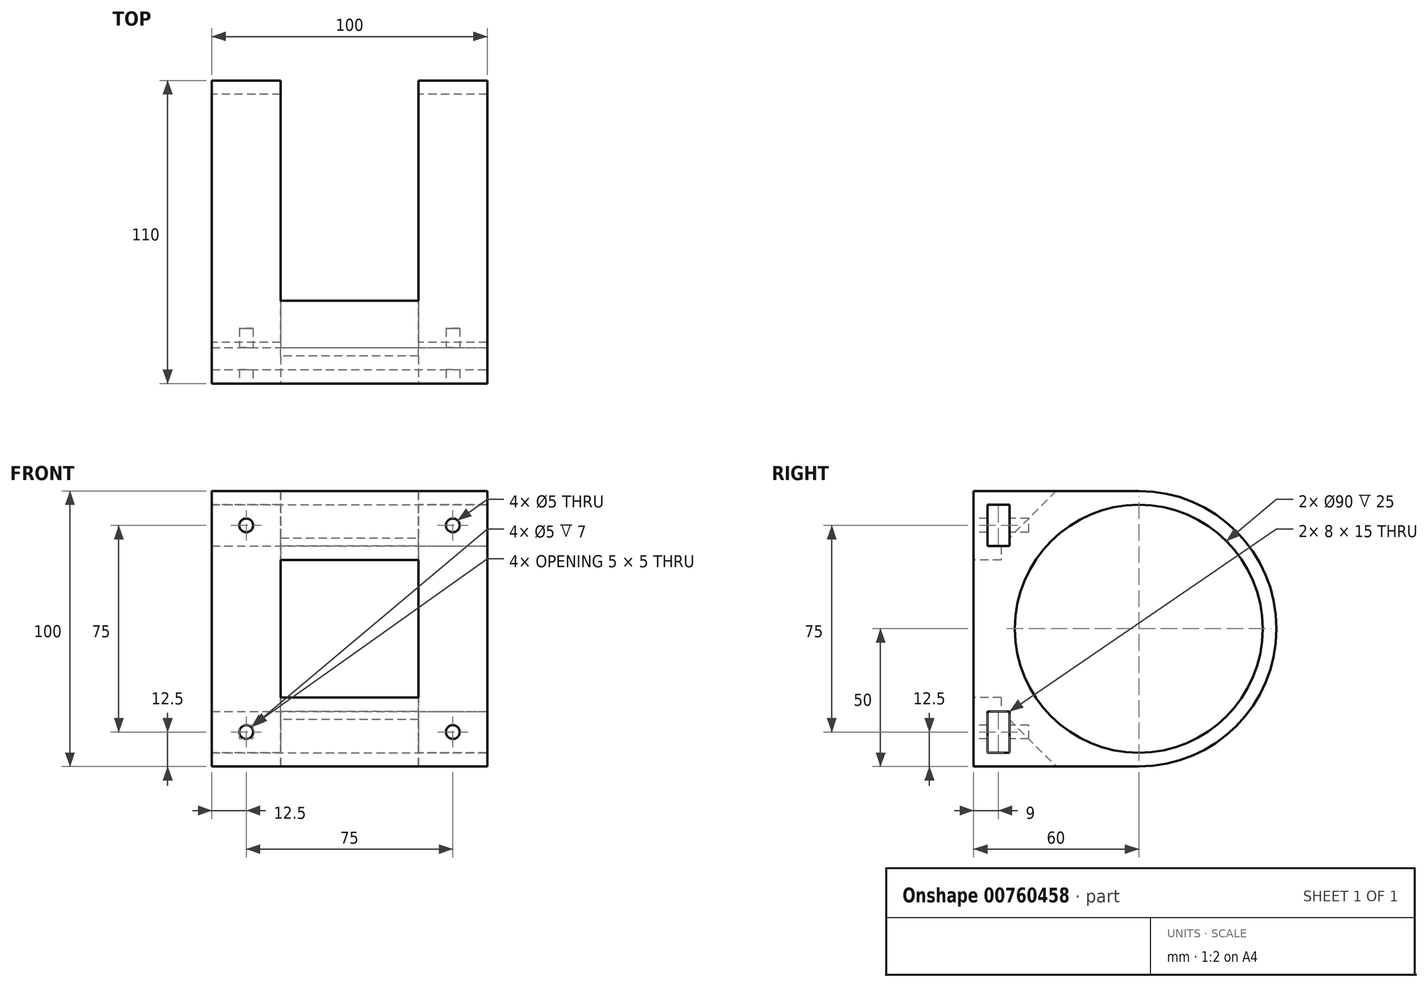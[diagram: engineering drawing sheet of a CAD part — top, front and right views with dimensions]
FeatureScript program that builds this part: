
annotation { "Feature Type Name" : "Feature", "Feature Type Description" : "" }
export const myFeature = defineFeature(function(context is Context, id is Id, definition is map)
    precondition{}
    {
        {
            var Q0;
            Q0=qCreatedBy(makeId("Right.planeOp"),FACE);
            var sketch = newSketch(context, id + "F0", { "sketchPlane" : qUnion([Q0])});
            skCircle(sketch, "E0", {"center": v(0, 0) * mm, "radius": 50 * mm});
            skCircle(sketch, "E1", {"center": v(0, 0) * mm, "radius": 40 * mm});
            skCircle(sketch, "E2", {"center": v(0, 0) * mm, "radius": 45 * mm});
            skLineSegment(sketch, "E3", {"start": v(-45, 0) * mm, "end": v(45, 0) * mm});
            skLineSegment(sketch, "E4.1.0", {"start": v(-44.14, -8.78) * mm, "end": v(44.14, 8.78) * mm});
            skLineSegment(sketch, "E4.2.0", {"start": v(-41.57, -17.22) * mm, "end": v(41.57, 17.22) * mm});
            skLineSegment(sketch, "E4.3.0", {"start": v(-37.42, -25) * mm, "end": v(37.42, 25) * mm});
            skLineSegment(sketch, "E4.4.0", {"start": v(-31.82, -31.82) * mm, "end": v(31.82, 31.82) * mm});
            skLineSegment(sketch, "E4.5.0", {"start": v(-25, -37.42) * mm, "end": v(25, 37.42) * mm});
            skLineSegment(sketch, "E4.6.0", {"start": v(-17.22, -41.57) * mm, "end": v(17.22, 41.57) * mm});
            skLineSegment(sketch, "E4.7.0", {"start": v(-8.78, -44.14) * mm, "end": v(8.78, 44.14) * mm});
            skLineSegment(sketch, "E4.8.0", {"start": v(0, -45) * mm, "end": v(0, 45) * mm});
            skLineSegment(sketch, "E4.9.0", {"start": v(8.78, -44.14) * mm, "end": v(-8.78, 44.14) * mm});
            skLineSegment(sketch, "E4.10.0", {"start": v(17.22, -41.57) * mm, "end": v(-17.22, 41.57) * mm});
            skLineSegment(sketch, "E4.11.0", {"start": v(25, -37.42) * mm, "end": v(-25, 37.42) * mm});
            skLineSegment(sketch, "E4.12.0", {"start": v(31.82, -31.82) * mm, "end": v(-31.82, 31.82) * mm});
            skLineSegment(sketch, "E4.13.0", {"start": v(37.42, -25) * mm, "end": v(-37.42, 25) * mm});
            skLineSegment(sketch, "E4.14.0", {"start": v(41.57, -17.22) * mm, "end": v(-41.57, 17.22) * mm});
            skLineSegment(sketch, "E4.15.0", {"start": v(44.14, -8.78) * mm, "end": v(-44.14, 8.78) * mm});
            skLineSegment(sketch, "E4.16.0", {"start": v(45, 0) * mm, "end": v(-45, 0) * mm});
            skLineSegment(sketch, "E4.17.0", {"start": v(44.14, 8.78) * mm, "end": v(-44.14, -8.78) * mm});
            skLineSegment(sketch, "E4.18.0", {"start": v(41.57, 17.22) * mm, "end": v(-41.57, -17.22) * mm});
            skLineSegment(sketch, "E4.19.0", {"start": v(37.42, 25) * mm, "end": v(-37.42, -25) * mm});
            skLineSegment(sketch, "E4.20.0", {"start": v(31.82, 31.82) * mm, "end": v(-31.82, -31.82) * mm});
            skLineSegment(sketch, "E4.21.0", {"start": v(25, 37.42) * mm, "end": v(-25, -37.42) * mm});
            skLineSegment(sketch, "E4.22.0", {"start": v(17.22, 41.57) * mm, "end": v(-17.22, -41.57) * mm});
            skLineSegment(sketch, "E4.23.0", {"start": v(8.78, 44.14) * mm, "end": v(-8.78, -44.14) * mm});
            skLineSegment(sketch, "E4.24.0", {"start": v(0, 45) * mm, "end": v(0, -45) * mm});
            skLineSegment(sketch, "E4.25.0", {"start": v(-8.78, 44.14) * mm, "end": v(8.78, -44.14) * mm});
            skLineSegment(sketch, "E4.26.0", {"start": v(-17.22, 41.57) * mm, "end": v(17.22, -41.57) * mm});
            skLineSegment(sketch, "E4.27.0", {"start": v(-25, 37.42) * mm, "end": v(25, -37.42) * mm});
            skLineSegment(sketch, "E4.28.0", {"start": v(-31.82, 31.82) * mm, "end": v(31.82, -31.82) * mm});
            skLineSegment(sketch, "E4.29.0", {"start": v(-37.42, 25) * mm, "end": v(37.42, -25) * mm});
            skLineSegment(sketch, "E4.30.0", {"start": v(-41.57, 17.22) * mm, "end": v(41.57, -17.22) * mm});
            skLineSegment(sketch, "E4.31.0", {"start": v(-44.14, 8.78) * mm, "end": v(44.14, -8.78) * mm});
            skLineSegment(sketch, "E5.bottom", {"start": v(0, 50) * mm, "end": v(-60, 50) * mm});
            skLineSegment(sketch, "E5.top", {"start": v(0, -50) * mm, "end": v(-60, -50) * mm});
            skLineSegment(sketch, "E5.left", {"start": v(0, 50) * mm, "end": v(0, -50) * mm, "construction": true});
            skLineSegment(sketch, "E5.right", {"start": v(-60, 50) * mm, "end": v(-60, -50) * mm});
            skLineSegment(sketch, "E6", {"start": v(-50, 50) * mm, "end": v(-50, -50) * mm});
            skLineSegment(sketch, "E7", {"start": v(-30, 50) * mm, "end": v(-50, 30) * mm});
            skLineSegment(sketch, "E8", {"start": v(-50, -30) * mm, "end": v(-30, -50) * mm});
            skSolve(sketch);
        }
        {
            var Q0;
            {var subQ0=sQuery(id+"F0.wireOp",EDGE,"E5.bottom");Q0=makeQuery(id+"F0.imprint","IMPRINT",FACE,{"disambiguationData":[TD([[makeQuery(id+"F0.imprint","IMPRINT",EDGE,{"derivedFrom":subQ0}),1.0]])]});}
            var Q1;
            {var subQ15=sQuery(id+"F0.wireOp",EDGE,"E0");var subQ16=makeQuery(id+"F0.imprint","INTERSECT",VERTEX,{"derivedFrom":[subQ15,sQuery(id+"F0.wireOp",EDGE,"E5.bottom")]});Q1=makeQuery(id+"F0.imprint","IMPRINT",FACE,{"disambiguationData":[TD([[makeQuery(id+"F0.imprint","IMPRINT",EDGE,{"disambiguationData":[TD([[subQ16,-1.0]])],"derivedFrom":subQ15}),1.0]])]});}
            var Q2;
            {var subQ0=sQuery(id+"F0.wireOp",EDGE,"E4.25.0");var subQ1=sQuery(id+"F0.wireOp",EDGE,"E1");var subQ2=makeQuery(id+"F0.imprint","INTERSECT",VERTEX,{"disambiguationData":[OD(0.0)],"derivedFrom":[subQ1,subQ0]});Q2=makeQuery(id+"F0.imprint","IMPRINT",FACE,{"disambiguationData":[TD([[makeQuery(id+"F0.imprint","IMPRINT",EDGE,{"disambiguationData":[TD([[subQ2,-1.0]])],"derivedFrom":subQ1}),-1.0]])]});}
            var Q3;
            {var subQ0=sQuery(id+"F0.wireOp",EDGE,"E4.26.0");var subQ1=sQuery(id+"F0.wireOp",EDGE,"E1");var subQ2=makeQuery(id+"F0.imprint","INTERSECT",VERTEX,{"disambiguationData":[OD(0.0)],"derivedFrom":[subQ1,subQ0]});Q3=makeQuery(id+"F0.imprint","IMPRINT",FACE,{"disambiguationData":[TD([[makeQuery(id+"F0.imprint","IMPRINT",EDGE,{"disambiguationData":[TD([[subQ2,-1.0]])],"derivedFrom":subQ1}),-1.0]])]});}
            var Q4;
            {var subQ0=sQuery(id+"F0.wireOp",EDGE,"E4.29.0");var subQ1=sQuery(id+"F0.wireOp",EDGE,"E1");var subQ2=makeQuery(id+"F0.imprint","INTERSECT",VERTEX,{"disambiguationData":[OD(0.0)],"derivedFrom":[subQ1,subQ0]});Q4=makeQuery(id+"F0.imprint","IMPRINT",FACE,{"disambiguationData":[TD([[makeQuery(id+"F0.imprint","IMPRINT",EDGE,{"disambiguationData":[TD([[subQ2,-1.0]])],"derivedFrom":subQ1}),-1.0]])]});}
            var Q5;
            {var subQ0=sQuery(id+"F0.wireOp",EDGE,"E4.30.0");var subQ1=sQuery(id+"F0.wireOp",EDGE,"E1");var subQ2=makeQuery(id+"F0.imprint","INTERSECT",VERTEX,{"disambiguationData":[OD(0.0)],"derivedFrom":[subQ1,subQ0]});Q5=makeQuery(id+"F0.imprint","IMPRINT",FACE,{"disambiguationData":[TD([[makeQuery(id+"F0.imprint","IMPRINT",EDGE,{"disambiguationData":[TD([[subQ2,-1.0]])],"derivedFrom":subQ1}),-1.0]])]});}
            var Q6;
            {var subQ0=sQuery(id+"F0.wireOp",EDGE,"E4.17.0");var subQ1=sQuery(id+"F0.wireOp",EDGE,"E1");var subQ2=makeQuery(id+"F0.imprint","INTERSECT",VERTEX,{"disambiguationData":[OD(1.0)],"derivedFrom":[subQ1,subQ0]});Q6=makeQuery(id+"F0.imprint","IMPRINT",FACE,{"disambiguationData":[TD([[makeQuery(id+"F0.imprint","IMPRINT",EDGE,{"disambiguationData":[TD([[subQ2,-1.0]])],"derivedFrom":subQ1}),-1.0]])]});}
            var Q7;
            {var subQ0=sQuery(id+"F0.wireOp",EDGE,"E4.18.0");var subQ1=sQuery(id+"F0.wireOp",EDGE,"E1");var subQ2=makeQuery(id+"F0.imprint","INTERSECT",VERTEX,{"disambiguationData":[OD(1.0)],"derivedFrom":[subQ1,subQ0]});Q7=makeQuery(id+"F0.imprint","IMPRINT",FACE,{"disambiguationData":[TD([[makeQuery(id+"F0.imprint","IMPRINT",EDGE,{"disambiguationData":[TD([[subQ2,-1.0]])],"derivedFrom":subQ1}),-1.0]])]});}
            var Q8;
            {var subQ0=sQuery(id+"F0.wireOp",EDGE,"E4.21.0");var subQ1=sQuery(id+"F0.wireOp",EDGE,"E1");var subQ2=makeQuery(id+"F0.imprint","INTERSECT",VERTEX,{"disambiguationData":[OD(1.0)],"derivedFrom":[subQ1,subQ0]});Q8=makeQuery(id+"F0.imprint","IMPRINT",FACE,{"disambiguationData":[TD([[makeQuery(id+"F0.imprint","IMPRINT",EDGE,{"disambiguationData":[TD([[subQ2,-1.0]])],"derivedFrom":subQ1}),-1.0]])]});}
            var Q9;
            {var subQ0=sQuery(id+"F0.wireOp",EDGE,"E4.22.0");var subQ1=sQuery(id+"F0.wireOp",EDGE,"E1");var subQ2=makeQuery(id+"F0.imprint","INTERSECT",VERTEX,{"disambiguationData":[OD(1.0)],"derivedFrom":[subQ1,subQ0]});Q9=makeQuery(id+"F0.imprint","IMPRINT",FACE,{"disambiguationData":[TD([[makeQuery(id+"F0.imprint","IMPRINT",EDGE,{"disambiguationData":[TD([[subQ2,-1.0]])],"derivedFrom":subQ1}),-1.0]])]});}
            var Q10;
            {var subQ0=sQuery(id+"F0.wireOp",EDGE,"E4.25.0");var subQ1=sQuery(id+"F0.wireOp",EDGE,"E1");var subQ2=makeQuery(id+"F0.imprint","INTERSECT",VERTEX,{"disambiguationData":[OD(1.0)],"derivedFrom":[subQ1,subQ0]});Q10=makeQuery(id+"F0.imprint","IMPRINT",FACE,{"disambiguationData":[TD([[makeQuery(id+"F0.imprint","IMPRINT",EDGE,{"disambiguationData":[TD([[subQ2,-1.0]])],"derivedFrom":subQ1}),-1.0]])]});}
            var Q11;
            {var subQ0=sQuery(id+"F0.wireOp",EDGE,"E4.26.0");var subQ1=sQuery(id+"F0.wireOp",EDGE,"E1");var subQ2=makeQuery(id+"F0.imprint","INTERSECT",VERTEX,{"disambiguationData":[OD(1.0)],"derivedFrom":[subQ1,subQ0]});Q11=makeQuery(id+"F0.imprint","IMPRINT",FACE,{"disambiguationData":[TD([[makeQuery(id+"F0.imprint","IMPRINT",EDGE,{"disambiguationData":[TD([[subQ2,-1.0]])],"derivedFrom":subQ1}),-1.0]])]});}
            var Q12;
            {var subQ0=sQuery(id+"F0.wireOp",EDGE,"E4.29.0");var subQ1=sQuery(id+"F0.wireOp",EDGE,"E1");var subQ2=makeQuery(id+"F0.imprint","INTERSECT",VERTEX,{"disambiguationData":[OD(1.0)],"derivedFrom":[subQ1,subQ0]});Q12=makeQuery(id+"F0.imprint","IMPRINT",FACE,{"disambiguationData":[TD([[makeQuery(id+"F0.imprint","IMPRINT",EDGE,{"disambiguationData":[TD([[subQ2,-1.0]])],"derivedFrom":subQ1}),-1.0]])]});}
            var Q13;
            {var subQ0=sQuery(id+"F0.wireOp",EDGE,"E4.30.0");var subQ1=sQuery(id+"F0.wireOp",EDGE,"E1");var subQ2=makeQuery(id+"F0.imprint","INTERSECT",VERTEX,{"disambiguationData":[OD(1.0)],"derivedFrom":[subQ1,subQ0]});Q13=makeQuery(id+"F0.imprint","IMPRINT",FACE,{"disambiguationData":[TD([[makeQuery(id+"F0.imprint","IMPRINT",EDGE,{"disambiguationData":[TD([[subQ2,-1.0]])],"derivedFrom":subQ1}),-1.0]])]});}
            var Q14;
            {var subQ0=sQuery(id+"F0.wireOp",EDGE,"E4.17.0");var subQ1=sQuery(id+"F0.wireOp",EDGE,"E1");var subQ2=makeQuery(id+"F0.imprint","INTERSECT",VERTEX,{"disambiguationData":[OD(0.0)],"derivedFrom":[subQ1,subQ0]});Q14=makeQuery(id+"F0.imprint","IMPRINT",FACE,{"disambiguationData":[TD([[makeQuery(id+"F0.imprint","IMPRINT",EDGE,{"disambiguationData":[TD([[subQ2,-1.0]])],"derivedFrom":subQ1}),-1.0]])]});}
            var Q15;
            {var subQ0=sQuery(id+"F0.wireOp",EDGE,"E4.18.0");var subQ1=sQuery(id+"F0.wireOp",EDGE,"E1");var subQ2=makeQuery(id+"F0.imprint","INTERSECT",VERTEX,{"disambiguationData":[OD(0.0)],"derivedFrom":[subQ1,subQ0]});Q15=makeQuery(id+"F0.imprint","IMPRINT",FACE,{"disambiguationData":[TD([[makeQuery(id+"F0.imprint","IMPRINT",EDGE,{"disambiguationData":[TD([[subQ2,-1.0]])],"derivedFrom":subQ1}),-1.0]])]});}
            var Q16;
            {var subQ0=sQuery(id+"F0.wireOp",EDGE,"E4.21.0");var subQ1=sQuery(id+"F0.wireOp",EDGE,"E1");var subQ2=makeQuery(id+"F0.imprint","INTERSECT",VERTEX,{"disambiguationData":[OD(0.0)],"derivedFrom":[subQ1,subQ0]});Q16=makeQuery(id+"F0.imprint","IMPRINT",FACE,{"disambiguationData":[TD([[makeQuery(id+"F0.imprint","IMPRINT",EDGE,{"disambiguationData":[TD([[subQ2,-1.0]])],"derivedFrom":subQ1}),-1.0]])]});}
            var Q17;
            {var subQ0=sQuery(id+"F0.wireOp",EDGE,"E4.22.0");var subQ1=sQuery(id+"F0.wireOp",EDGE,"E1");var subQ2=makeQuery(id+"F0.imprint","INTERSECT",VERTEX,{"disambiguationData":[OD(0.0)],"derivedFrom":[subQ1,subQ0]});Q17=makeQuery(id+"F0.imprint","IMPRINT",FACE,{"disambiguationData":[TD([[makeQuery(id+"F0.imprint","IMPRINT",EDGE,{"disambiguationData":[TD([[subQ2,-1.0]])],"derivedFrom":subQ1}),-1.0]])]});}
            var Q18;
            {var subQ4=sQuery(id+"F0.wireOp",EDGE,"E5.right");Q18=makeQuery(id+"F0.imprint","IMPRINT",FACE,{"disambiguationData":[TD([[makeQuery(id+"F0.imprint","IMPRINT",EDGE,{"derivedFrom":subQ4}),1.0]])]});}
            var Q19;
            {var subQ0=sQuery(id+"F0.wireOp",EDGE,"E5.top");var subQ1=sQuery(id+"F0.wireOp",EDGE,"E0");var subQ2=makeQuery(id+"F0.imprint","INTERSECT",VERTEX,{"derivedFrom":[subQ1,subQ0]});Q19=makeQuery(id+"F0.imprint","IMPRINT",FACE,{"disambiguationData":[TD([[makeQuery(id+"F0.imprint","IMPRINT",EDGE,{"disambiguationData":[TD([[subQ2,1.0]])],"derivedFrom":subQ1}),-1.0]])]});}
            var Q20;
            {var subQ5=sQuery(id+"F0.wireOp",EDGE,"E7");Q20=makeQuery(id+"F0.imprint","IMPRINT",FACE,{"disambiguationData":[TD([[makeQuery(id+"F0.imprint","IMPRINT",EDGE,{"derivedFrom":subQ5}),1.0]])]});}
            var Q21;
            {var subQ3=sQuery(id+"F0.wireOp",EDGE,"E8");Q21=makeQuery(id+"F0.imprint","IMPRINT",FACE,{"disambiguationData":[TD([[makeQuery(id+"F0.imprint","IMPRINT",EDGE,{"derivedFrom":subQ3}),-1.0]])]});}
            extrude(context, id + "F1", {"entities" : qUnion([Q0, Q1, Q2, Q3, Q4, Q5, Q6, Q7, Q8, Q9, Q10, Q11, Q12, Q13, Q14, Q15, Q16, Q17, Q18, Q19, Q20, Q21]), "endBound" : BoundingType.SYMMETRIC, "depth" : 100 * mm, "offsetDistance" : 25 * mm});
        }
        {
            var Q0;
            {var subQ15=sQuery(id+"F0.wireOp",EDGE,"E0");var subQ16=makeQuery(id+"F0.imprint","INTERSECT",VERTEX,{"derivedFrom":[subQ15,sQuery(id+"F0.wireOp",EDGE,"E5.bottom")]});Q0=makeQuery(id+"F0.imprint","IMPRINT",FACE,{"disambiguationData":[TD([[makeQuery(id+"F0.imprint","IMPRINT",EDGE,{"disambiguationData":[TD([[subQ16,-1.0]])],"derivedFrom":subQ15}),1.0]])]});}
            var Q1;
            {var subQ0=sQuery(id+"F0.wireOp",EDGE,"E4.23.0");var subQ1=sQuery(id+"F0.wireOp",EDGE,"E1");var subQ2=makeQuery(id+"F0.imprint","INTERSECT",VERTEX,{"disambiguationData":[OD(1.0)],"derivedFrom":[subQ1,subQ0]});Q1=makeQuery(id+"F0.imprint","IMPRINT",FACE,{"disambiguationData":[TD([[makeQuery(id+"F0.imprint","IMPRINT",EDGE,{"disambiguationData":[TD([[subQ2,-1.0]])],"derivedFrom":subQ1}),-1.0]])]});}
            var Q2;
            {var subQ0=sQuery(id+"F0.wireOp",EDGE,"E4.17.0");var subQ1=sQuery(id+"F0.wireOp",EDGE,"E1");var subQ2=makeQuery(id+"F0.imprint","INTERSECT",VERTEX,{"disambiguationData":[OD(0.0)],"derivedFrom":[subQ1,subQ0]});Q2=makeQuery(id+"F0.imprint","IMPRINT",FACE,{"disambiguationData":[TD([[makeQuery(id+"F0.imprint","IMPRINT",EDGE,{"disambiguationData":[TD([[subQ2,1.0]])],"derivedFrom":subQ1}),1.0]])]});}
            var Q3;
            {var subQ0=sQuery(id+"F0.wireOp",EDGE,"E4.16.0");var subQ1=sQuery(id+"F0.wireOp",EDGE,"E1");var subQ2=makeQuery(id+"F0.imprint","INTERSECT",VERTEX,{"disambiguationData":[OD(0.0)],"derivedFrom":[subQ1,subQ0]});Q3=makeQuery(id+"F0.imprint","IMPRINT",FACE,{"disambiguationData":[TD([[makeQuery(id+"F0.imprint","IMPRINT",EDGE,{"disambiguationData":[TD([[subQ2,1.0]])],"derivedFrom":subQ1}),1.0]])]});}
            var Q4;
            {var subQ0=sQuery(id+"F0.wireOp",EDGE,"E4.17.0");var subQ1=sQuery(id+"F0.wireOp",EDGE,"E1");var subQ2=makeQuery(id+"F0.imprint","INTERSECT",VERTEX,{"disambiguationData":[OD(0.0)],"derivedFrom":[subQ1,subQ0]});Q4=makeQuery(id+"F0.imprint","IMPRINT",FACE,{"disambiguationData":[TD([[makeQuery(id+"F0.imprint","IMPRINT",EDGE,{"disambiguationData":[TD([[subQ2,-1.0]])],"derivedFrom":subQ1}),1.0]])]});}
            var Q5;
            {var subQ0=sQuery(id+"F0.wireOp",EDGE,"E4.26.0");var subQ1=sQuery(id+"F0.wireOp",EDGE,"E1");var subQ2=makeQuery(id+"F0.imprint","INTERSECT",VERTEX,{"disambiguationData":[OD(0.0)],"derivedFrom":[subQ1,subQ0]});Q5=makeQuery(id+"F0.imprint","IMPRINT",FACE,{"disambiguationData":[TD([[makeQuery(id+"F0.imprint","IMPRINT",EDGE,{"disambiguationData":[TD([[subQ2,-1.0]])],"derivedFrom":subQ1}),-1.0]])]});}
            var Q6;
            {var subQ0=sQuery(id+"F0.wireOp",EDGE,"E4.28.0");var subQ1=sQuery(id+"F0.wireOp",EDGE,"E1");var subQ2=makeQuery(id+"F0.imprint","INTERSECT",VERTEX,{"disambiguationData":[OD(0.0)],"derivedFrom":[subQ1,subQ0]});Q6=makeQuery(id+"F0.imprint","IMPRINT",FACE,{"disambiguationData":[TD([[makeQuery(id+"F0.imprint","IMPRINT",EDGE,{"disambiguationData":[TD([[subQ2,-1.0]])],"derivedFrom":subQ1}),-1.0]])]});}
            var Q7;
            {var subQ0=sQuery(id+"F0.wireOp",EDGE,"E4.18.0");var subQ1=sQuery(id+"F0.wireOp",EDGE,"E1");var subQ2=makeQuery(id+"F0.imprint","INTERSECT",VERTEX,{"disambiguationData":[OD(1.0)],"derivedFrom":[subQ1,subQ0]});Q7=makeQuery(id+"F0.imprint","IMPRINT",FACE,{"disambiguationData":[TD([[makeQuery(id+"F0.imprint","IMPRINT",EDGE,{"disambiguationData":[TD([[subQ2,-1.0]])],"derivedFrom":subQ1}),-1.0]])]});}
            var Q8;
            {var subQ0=sQuery(id+"F0.wireOp",EDGE,"E4.25.0");var subQ1=sQuery(id+"F0.wireOp",EDGE,"E1");var subQ2=makeQuery(id+"F0.imprint","INTERSECT",VERTEX,{"disambiguationData":[OD(0.0)],"derivedFrom":[subQ1,subQ0]});Q8=makeQuery(id+"F0.imprint","IMPRINT",FACE,{"disambiguationData":[TD([[makeQuery(id+"F0.imprint","IMPRINT",EDGE,{"disambiguationData":[TD([[subQ2,-1.0]])],"derivedFrom":subQ1}),1.0]])]});}
            var Q9;
            {var subQ0=sQuery(id+"F0.wireOp",EDGE,"E4.28.0");var subQ1=sQuery(id+"F0.wireOp",EDGE,"E1");var subQ2=makeQuery(id+"F0.imprint","INTERSECT",VERTEX,{"disambiguationData":[OD(1.0)],"derivedFrom":[subQ1,subQ0]});Q9=makeQuery(id+"F0.imprint","IMPRINT",FACE,{"disambiguationData":[TD([[makeQuery(id+"F0.imprint","IMPRINT",EDGE,{"disambiguationData":[TD([[subQ2,-1.0]])],"derivedFrom":subQ1}),-1.0]])]});}
            var Q10;
            {var subQ0=sQuery(id+"F0.wireOp",EDGE,"E4.31.0");var subQ1=sQuery(id+"F0.wireOp",EDGE,"E1");var subQ2=makeQuery(id+"F0.imprint","INTERSECT",VERTEX,{"disambiguationData":[OD(0.0)],"derivedFrom":[subQ1,subQ0]});Q10=makeQuery(id+"F0.imprint","IMPRINT",FACE,{"disambiguationData":[TD([[makeQuery(id+"F0.imprint","IMPRINT",EDGE,{"disambiguationData":[TD([[subQ2,-1.0]])],"derivedFrom":subQ1}),-1.0]])]});}
            var Q11;
            {var subQ0=sQuery(id+"F0.wireOp",EDGE,"E4.20.0");var subQ1=sQuery(id+"F0.wireOp",EDGE,"E1");var subQ2=makeQuery(id+"F0.imprint","INTERSECT",VERTEX,{"disambiguationData":[OD(0.0)],"derivedFrom":[subQ1,subQ0]});Q11=makeQuery(id+"F0.imprint","IMPRINT",FACE,{"disambiguationData":[TD([[makeQuery(id+"F0.imprint","IMPRINT",EDGE,{"disambiguationData":[TD([[subQ2,-1.0]])],"derivedFrom":subQ1}),-1.0]])]});}
            var Q12;
            {var subQ0=sQuery(id+"F0.wireOp",EDGE,"E4.17.0");var subQ1=sQuery(id+"F0.wireOp",EDGE,"E1");var subQ2=makeQuery(id+"F0.imprint","INTERSECT",VERTEX,{"disambiguationData":[OD(0.0)],"derivedFrom":[subQ1,subQ0]});Q12=makeQuery(id+"F0.imprint","IMPRINT",FACE,{"disambiguationData":[TD([[makeQuery(id+"F0.imprint","IMPRINT",EDGE,{"disambiguationData":[TD([[subQ2,-1.0]])],"derivedFrom":subQ1}),-1.0]])]});}
            var Q13;
            {var subQ0=sQuery(id+"F0.wireOp",EDGE,"E4.24.0");var subQ1=sQuery(id+"F0.wireOp",EDGE,"E1");var subQ2=makeQuery(id+"F0.imprint","INTERSECT",VERTEX,{"disambiguationData":[OD(1.0)],"derivedFrom":[subQ1,subQ0]});Q13=makeQuery(id+"F0.imprint","IMPRINT",FACE,{"disambiguationData":[TD([[makeQuery(id+"F0.imprint","IMPRINT",EDGE,{"disambiguationData":[TD([[subQ2,-1.0]])],"derivedFrom":subQ1}),-1.0]])]});}
            var Q14;
            {var subQ0=sQuery(id+"F0.wireOp",EDGE,"E4.16.0");var subQ1=sQuery(id+"F0.wireOp",EDGE,"E1");var subQ2=makeQuery(id+"F0.imprint","INTERSECT",VERTEX,{"disambiguationData":[OD(1.0)],"derivedFrom":[subQ1,subQ0]});Q14=makeQuery(id+"F0.imprint","IMPRINT",FACE,{"disambiguationData":[TD([[makeQuery(id+"F0.imprint","IMPRINT",EDGE,{"disambiguationData":[TD([[subQ2,-1.0]])],"derivedFrom":subQ1}),1.0]])]});}
            var Q15;
            {var subQ0=sQuery(id+"F0.wireOp",EDGE,"E4.17.0");var subQ1=sQuery(id+"F0.wireOp",EDGE,"E1");var subQ2=makeQuery(id+"F0.imprint","INTERSECT",VERTEX,{"disambiguationData":[OD(0.0)],"derivedFrom":[subQ1,subQ0]});Q15=makeQuery(id+"F0.imprint","IMPRINT",FACE,{"disambiguationData":[TD([[makeQuery(id+"F0.imprint","IMPRINT",EDGE,{"disambiguationData":[TD([[subQ2,1.0]])],"derivedFrom":subQ1}),-1.0]])]});}
            var Q16;
            {var subQ0=sQuery(id+"F0.wireOp",EDGE,"E4.22.0");var subQ1=sQuery(id+"F0.wireOp",EDGE,"E1");var subQ2=makeQuery(id+"F0.imprint","INTERSECT",VERTEX,{"disambiguationData":[OD(1.0)],"derivedFrom":[subQ1,subQ0]});Q16=makeQuery(id+"F0.imprint","IMPRINT",FACE,{"disambiguationData":[TD([[makeQuery(id+"F0.imprint","IMPRINT",EDGE,{"disambiguationData":[TD([[subQ2,-1.0]])],"derivedFrom":subQ1}),-1.0]])]});}
            var Q17;
            {var subQ0=sQuery(id+"F0.wireOp",EDGE,"E4.25.0");var subQ1=sQuery(id+"F0.wireOp",EDGE,"E1");var subQ2=makeQuery(id+"F0.imprint","INTERSECT",VERTEX,{"disambiguationData":[OD(1.0)],"derivedFrom":[subQ1,subQ0]});Q17=makeQuery(id+"F0.imprint","IMPRINT",FACE,{"disambiguationData":[TD([[makeQuery(id+"F0.imprint","IMPRINT",EDGE,{"disambiguationData":[TD([[subQ2,-1.0]])],"derivedFrom":subQ1}),1.0]])]});}
            var Q18;
            {var subQ0=sQuery(id+"F0.wireOp",EDGE,"E4.24.0");var subQ1=sQuery(id+"F0.wireOp",EDGE,"E1");var subQ2=makeQuery(id+"F0.imprint","INTERSECT",VERTEX,{"disambiguationData":[OD(0.0)],"derivedFrom":[subQ1,subQ0]});Q18=makeQuery(id+"F0.imprint","IMPRINT",FACE,{"disambiguationData":[TD([[makeQuery(id+"F0.imprint","IMPRINT",EDGE,{"disambiguationData":[TD([[subQ2,-1.0]])],"derivedFrom":subQ1}),1.0]])]});}
            var Q19;
            {var subQ0=sQuery(id+"F0.wireOp",EDGE,"E4.26.0");var subQ1=sQuery(id+"F0.wireOp",EDGE,"E1");var subQ2=makeQuery(id+"F0.imprint","INTERSECT",VERTEX,{"disambiguationData":[OD(0.0)],"derivedFrom":[subQ1,subQ0]});Q19=makeQuery(id+"F0.imprint","IMPRINT",FACE,{"disambiguationData":[TD([[makeQuery(id+"F0.imprint","IMPRINT",EDGE,{"disambiguationData":[TD([[subQ2,-1.0]])],"derivedFrom":subQ1}),1.0]])]});}
            var Q20;
            {var subQ0=sQuery(id+"F0.wireOp",EDGE,"E4.21.0");var subQ1=sQuery(id+"F0.wireOp",EDGE,"E1");var subQ2=makeQuery(id+"F0.imprint","INTERSECT",VERTEX,{"disambiguationData":[OD(1.0)],"derivedFrom":[subQ1,subQ0]});Q20=makeQuery(id+"F0.imprint","IMPRINT",FACE,{"disambiguationData":[TD([[makeQuery(id+"F0.imprint","IMPRINT",EDGE,{"disambiguationData":[TD([[subQ2,-1.0]])],"derivedFrom":subQ1}),-1.0]])]});}
            var Q21;
            {var subQ0=sQuery(id+"F0.wireOp",EDGE,"E4.28.0");var subQ1=sQuery(id+"F0.wireOp",EDGE,"E1");var subQ2=makeQuery(id+"F0.imprint","INTERSECT",VERTEX,{"disambiguationData":[OD(1.0)],"derivedFrom":[subQ1,subQ0]});Q21=makeQuery(id+"F0.imprint","IMPRINT",FACE,{"disambiguationData":[TD([[makeQuery(id+"F0.imprint","IMPRINT",EDGE,{"disambiguationData":[TD([[subQ2,-1.0]])],"derivedFrom":subQ1}),1.0]])]});}
            var Q22;
            {var subQ0=sQuery(id+"F0.wireOp",EDGE,"E4.19.0");var subQ1=sQuery(id+"F0.wireOp",EDGE,"E1");var subQ2=makeQuery(id+"F0.imprint","INTERSECT",VERTEX,{"disambiguationData":[OD(1.0)],"derivedFrom":[subQ1,subQ0]});Q22=makeQuery(id+"F0.imprint","IMPRINT",FACE,{"disambiguationData":[TD([[makeQuery(id+"F0.imprint","IMPRINT",EDGE,{"disambiguationData":[TD([[subQ2,-1.0]])],"derivedFrom":subQ1}),-1.0]])]});}
            var Q23;
            {var subQ0=sQuery(id+"F0.wireOp",EDGE,"E4.19.0");var subQ1=sQuery(id+"F0.wireOp",EDGE,"E1");var subQ2=makeQuery(id+"F0.imprint","INTERSECT",VERTEX,{"disambiguationData":[OD(0.0)],"derivedFrom":[subQ1,subQ0]});Q23=makeQuery(id+"F0.imprint","IMPRINT",FACE,{"disambiguationData":[TD([[makeQuery(id+"F0.imprint","IMPRINT",EDGE,{"disambiguationData":[TD([[subQ2,-1.0]])],"derivedFrom":subQ1}),-1.0]])]});}
            var Q24;
            {var subQ0=sQuery(id+"F0.wireOp",EDGE,"E4.18.0");var subQ1=sQuery(id+"F0.wireOp",EDGE,"E1");var subQ2=makeQuery(id+"F0.imprint","INTERSECT",VERTEX,{"disambiguationData":[OD(0.0)],"derivedFrom":[subQ1,subQ0]});Q24=makeQuery(id+"F0.imprint","IMPRINT",FACE,{"disambiguationData":[TD([[makeQuery(id+"F0.imprint","IMPRINT",EDGE,{"disambiguationData":[TD([[subQ2,-1.0]])],"derivedFrom":subQ1}),1.0]])]});}
            var Q25;
            {var subQ0=sQuery(id+"F0.wireOp",EDGE,"E4.22.0");var subQ1=sQuery(id+"F0.wireOp",EDGE,"E1");var subQ2=makeQuery(id+"F0.imprint","INTERSECT",VERTEX,{"disambiguationData":[OD(1.0)],"derivedFrom":[subQ1,subQ0]});Q25=makeQuery(id+"F0.imprint","IMPRINT",FACE,{"disambiguationData":[TD([[makeQuery(id+"F0.imprint","IMPRINT",EDGE,{"disambiguationData":[TD([[subQ2,-1.0]])],"derivedFrom":subQ1}),1.0]])]});}
            var Q26;
            {var subQ0=sQuery(id+"F0.wireOp",EDGE,"E4.18.0");var subQ1=sQuery(id+"F0.wireOp",EDGE,"E1");var subQ2=makeQuery(id+"F0.imprint","INTERSECT",VERTEX,{"disambiguationData":[OD(0.0)],"derivedFrom":[subQ1,subQ0]});Q26=makeQuery(id+"F0.imprint","IMPRINT",FACE,{"disambiguationData":[TD([[makeQuery(id+"F0.imprint","IMPRINT",EDGE,{"disambiguationData":[TD([[subQ2,-1.0]])],"derivedFrom":subQ1}),-1.0]])]});}
            var Q27;
            {var subQ0=sQuery(id+"F0.wireOp",EDGE,"E4.25.0");var subQ1=sQuery(id+"F0.wireOp",EDGE,"E1");var subQ2=makeQuery(id+"F0.imprint","INTERSECT",VERTEX,{"disambiguationData":[OD(1.0)],"derivedFrom":[subQ1,subQ0]});Q27=makeQuery(id+"F0.imprint","IMPRINT",FACE,{"disambiguationData":[TD([[makeQuery(id+"F0.imprint","IMPRINT",EDGE,{"disambiguationData":[TD([[subQ2,-1.0]])],"derivedFrom":subQ1}),-1.0]])]});}
            var Q28;
            {var subQ0=sQuery(id+"F0.wireOp",EDGE,"E4.16.0");var subQ1=sQuery(id+"F0.wireOp",EDGE,"E1");var subQ2=makeQuery(id+"F0.imprint","INTERSECT",VERTEX,{"disambiguationData":[OD(0.0)],"derivedFrom":[subQ1,subQ0]});Q28=makeQuery(id+"F0.imprint","IMPRINT",FACE,{"disambiguationData":[TD([[makeQuery(id+"F0.imprint","IMPRINT",EDGE,{"disambiguationData":[TD([[subQ2,1.0]])],"derivedFrom":subQ1}),-1.0]])]});}
            var Q29;
            {var subQ0=sQuery(id+"F0.wireOp",EDGE,"E4.29.0");var subQ1=sQuery(id+"F0.wireOp",EDGE,"E1");var subQ2=makeQuery(id+"F0.imprint","INTERSECT",VERTEX,{"disambiguationData":[OD(0.0)],"derivedFrom":[subQ1,subQ0]});Q29=makeQuery(id+"F0.imprint","IMPRINT",FACE,{"disambiguationData":[TD([[makeQuery(id+"F0.imprint","IMPRINT",EDGE,{"disambiguationData":[TD([[subQ2,-1.0]])],"derivedFrom":subQ1}),1.0]])]});}
            var Q30;
            {var subQ0=sQuery(id+"F0.wireOp",EDGE,"E4.28.0");var subQ1=sQuery(id+"F0.wireOp",EDGE,"E1");var subQ2=makeQuery(id+"F0.imprint","INTERSECT",VERTEX,{"disambiguationData":[OD(0.0)],"derivedFrom":[subQ1,subQ0]});Q30=makeQuery(id+"F0.imprint","IMPRINT",FACE,{"disambiguationData":[TD([[makeQuery(id+"F0.imprint","IMPRINT",EDGE,{"disambiguationData":[TD([[subQ2,-1.0]])],"derivedFrom":subQ1}),1.0]])]});}
            var Q31;
            {var subQ0=sQuery(id+"F0.wireOp",EDGE,"E4.31.0");var subQ1=sQuery(id+"F0.wireOp",EDGE,"E1");var subQ2=makeQuery(id+"F0.imprint","INTERSECT",VERTEX,{"disambiguationData":[OD(0.0)],"derivedFrom":[subQ1,subQ0]});Q31=makeQuery(id+"F0.imprint","IMPRINT",FACE,{"disambiguationData":[TD([[makeQuery(id+"F0.imprint","IMPRINT",EDGE,{"disambiguationData":[TD([[subQ2,-1.0]])],"derivedFrom":subQ1}),1.0]])]});}
            var Q32;
            {var subQ0=sQuery(id+"F0.wireOp",EDGE,"E4.21.0");var subQ1=sQuery(id+"F0.wireOp",EDGE,"E1");var subQ2=makeQuery(id+"F0.imprint","INTERSECT",VERTEX,{"disambiguationData":[OD(0.0)],"derivedFrom":[subQ1,subQ0]});Q32=makeQuery(id+"F0.imprint","IMPRINT",FACE,{"disambiguationData":[TD([[makeQuery(id+"F0.imprint","IMPRINT",EDGE,{"disambiguationData":[TD([[subQ2,-1.0]])],"derivedFrom":subQ1}),1.0]])]});}
            var Q33;
            {var subQ0=sQuery(id+"F0.wireOp",EDGE,"E4.29.0");var subQ1=sQuery(id+"F0.wireOp",EDGE,"E1");var subQ2=makeQuery(id+"F0.imprint","INTERSECT",VERTEX,{"disambiguationData":[OD(1.0)],"derivedFrom":[subQ1,subQ0]});Q33=makeQuery(id+"F0.imprint","IMPRINT",FACE,{"disambiguationData":[TD([[makeQuery(id+"F0.imprint","IMPRINT",EDGE,{"disambiguationData":[TD([[subQ2,-1.0]])],"derivedFrom":subQ1}),1.0]])]});}
            var Q34;
            {var subQ0=sQuery(id+"F0.wireOp",EDGE,"E4.29.0");var subQ1=sQuery(id+"F0.wireOp",EDGE,"E1");var subQ2=makeQuery(id+"F0.imprint","INTERSECT",VERTEX,{"disambiguationData":[OD(0.0)],"derivedFrom":[subQ1,subQ0]});Q34=makeQuery(id+"F0.imprint","IMPRINT",FACE,{"disambiguationData":[TD([[makeQuery(id+"F0.imprint","IMPRINT",EDGE,{"disambiguationData":[TD([[subQ2,-1.0]])],"derivedFrom":subQ1}),-1.0]])]});}
            var Q35;
            {var subQ0=sQuery(id+"F0.wireOp",EDGE,"E4.27.0");var subQ1=sQuery(id+"F0.wireOp",EDGE,"E1");var subQ2=makeQuery(id+"F0.imprint","INTERSECT",VERTEX,{"disambiguationData":[OD(0.0)],"derivedFrom":[subQ1,subQ0]});Q35=makeQuery(id+"F0.imprint","IMPRINT",FACE,{"disambiguationData":[TD([[makeQuery(id+"F0.imprint","IMPRINT",EDGE,{"disambiguationData":[TD([[subQ2,-1.0]])],"derivedFrom":subQ1}),-1.0]])]});}
            var Q36;
            {var subQ0=sQuery(id+"F0.wireOp",EDGE,"E4.27.0");var subQ1=sQuery(id+"F0.wireOp",EDGE,"E1");var subQ2=makeQuery(id+"F0.imprint","INTERSECT",VERTEX,{"disambiguationData":[OD(1.0)],"derivedFrom":[subQ1,subQ0]});Q36=makeQuery(id+"F0.imprint","IMPRINT",FACE,{"disambiguationData":[TD([[makeQuery(id+"F0.imprint","IMPRINT",EDGE,{"disambiguationData":[TD([[subQ2,-1.0]])],"derivedFrom":subQ1}),-1.0]])]});}
            var Q37;
            {var subQ0=sQuery(id+"F0.wireOp",EDGE,"E4.27.0");var subQ1=sQuery(id+"F0.wireOp",EDGE,"E1");var subQ2=makeQuery(id+"F0.imprint","INTERSECT",VERTEX,{"disambiguationData":[OD(1.0)],"derivedFrom":[subQ1,subQ0]});Q37=makeQuery(id+"F0.imprint","IMPRINT",FACE,{"disambiguationData":[TD([[makeQuery(id+"F0.imprint","IMPRINT",EDGE,{"disambiguationData":[TD([[subQ2,-1.0]])],"derivedFrom":subQ1}),1.0]])]});}
            var Q38;
            {var subQ0=sQuery(id+"F0.wireOp",EDGE,"E4.20.0");var subQ1=sQuery(id+"F0.wireOp",EDGE,"E1");var subQ2=makeQuery(id+"F0.imprint","INTERSECT",VERTEX,{"disambiguationData":[OD(1.0)],"derivedFrom":[subQ1,subQ0]});Q38=makeQuery(id+"F0.imprint","IMPRINT",FACE,{"disambiguationData":[TD([[makeQuery(id+"F0.imprint","IMPRINT",EDGE,{"disambiguationData":[TD([[subQ2,-1.0]])],"derivedFrom":subQ1}),-1.0]])]});}
            var Q39;
            {var subQ0=sQuery(id+"F0.wireOp",EDGE,"E4.26.0");var subQ1=sQuery(id+"F0.wireOp",EDGE,"E1");var subQ2=makeQuery(id+"F0.imprint","INTERSECT",VERTEX,{"disambiguationData":[OD(1.0)],"derivedFrom":[subQ1,subQ0]});Q39=makeQuery(id+"F0.imprint","IMPRINT",FACE,{"disambiguationData":[TD([[makeQuery(id+"F0.imprint","IMPRINT",EDGE,{"disambiguationData":[TD([[subQ2,-1.0]])],"derivedFrom":subQ1}),-1.0]])]});}
            var Q40;
            {var subQ0=sQuery(id+"F0.wireOp",EDGE,"E4.21.0");var subQ1=sQuery(id+"F0.wireOp",EDGE,"E1");var subQ2=makeQuery(id+"F0.imprint","INTERSECT",VERTEX,{"disambiguationData":[OD(1.0)],"derivedFrom":[subQ1,subQ0]});Q40=makeQuery(id+"F0.imprint","IMPRINT",FACE,{"disambiguationData":[TD([[makeQuery(id+"F0.imprint","IMPRINT",EDGE,{"disambiguationData":[TD([[subQ2,-1.0]])],"derivedFrom":subQ1}),1.0]])]});}
            var Q41;
            {var subQ0=sQuery(id+"F0.wireOp",EDGE,"E4.17.0");var subQ1=sQuery(id+"F0.wireOp",EDGE,"E1");var subQ2=makeQuery(id+"F0.imprint","INTERSECT",VERTEX,{"disambiguationData":[OD(1.0)],"derivedFrom":[subQ1,subQ0]});Q41=makeQuery(id+"F0.imprint","IMPRINT",FACE,{"disambiguationData":[TD([[makeQuery(id+"F0.imprint","IMPRINT",EDGE,{"disambiguationData":[TD([[subQ2,-1.0]])],"derivedFrom":subQ1}),-1.0]])]});}
            var Q42;
            {var subQ0=sQuery(id+"F0.wireOp",EDGE,"E4.17.0");var subQ1=sQuery(id+"F0.wireOp",EDGE,"E1");var subQ2=makeQuery(id+"F0.imprint","INTERSECT",VERTEX,{"disambiguationData":[OD(1.0)],"derivedFrom":[subQ1,subQ0]});Q42=makeQuery(id+"F0.imprint","IMPRINT",FACE,{"disambiguationData":[TD([[makeQuery(id+"F0.imprint","IMPRINT",EDGE,{"disambiguationData":[TD([[subQ2,-1.0]])],"derivedFrom":subQ1}),1.0]])]});}
            var Q43;
            {var subQ0=sQuery(id+"F0.wireOp",EDGE,"E4.30.0");var subQ1=sQuery(id+"F0.wireOp",EDGE,"E1");var subQ2=makeQuery(id+"F0.imprint","INTERSECT",VERTEX,{"disambiguationData":[OD(1.0)],"derivedFrom":[subQ1,subQ0]});Q43=makeQuery(id+"F0.imprint","IMPRINT",FACE,{"disambiguationData":[TD([[makeQuery(id+"F0.imprint","IMPRINT",EDGE,{"disambiguationData":[TD([[subQ2,-1.0]])],"derivedFrom":subQ1}),1.0]])]});}
            var Q44;
            {var subQ0=sQuery(id+"F0.wireOp",EDGE,"E4.22.0");var subQ1=sQuery(id+"F0.wireOp",EDGE,"E1");var subQ2=makeQuery(id+"F0.imprint","INTERSECT",VERTEX,{"disambiguationData":[OD(0.0)],"derivedFrom":[subQ1,subQ0]});Q44=makeQuery(id+"F0.imprint","IMPRINT",FACE,{"disambiguationData":[TD([[makeQuery(id+"F0.imprint","IMPRINT",EDGE,{"disambiguationData":[TD([[subQ2,-1.0]])],"derivedFrom":subQ1}),1.0]])]});}
            var Q45;
            {var subQ0=sQuery(id+"F0.wireOp",EDGE,"E4.27.0");var subQ1=sQuery(id+"F0.wireOp",EDGE,"E1");var subQ2=makeQuery(id+"F0.imprint","INTERSECT",VERTEX,{"disambiguationData":[OD(0.0)],"derivedFrom":[subQ1,subQ0]});Q45=makeQuery(id+"F0.imprint","IMPRINT",FACE,{"disambiguationData":[TD([[makeQuery(id+"F0.imprint","IMPRINT",EDGE,{"disambiguationData":[TD([[subQ2,-1.0]])],"derivedFrom":subQ1}),1.0]])]});}
            var Q46;
            {var subQ0=sQuery(id+"F0.wireOp",EDGE,"E4.23.0");var subQ1=sQuery(id+"F0.wireOp",EDGE,"E1");var subQ2=makeQuery(id+"F0.imprint","INTERSECT",VERTEX,{"disambiguationData":[OD(1.0)],"derivedFrom":[subQ1,subQ0]});Q46=makeQuery(id+"F0.imprint","IMPRINT",FACE,{"disambiguationData":[TD([[makeQuery(id+"F0.imprint","IMPRINT",EDGE,{"disambiguationData":[TD([[subQ2,-1.0]])],"derivedFrom":subQ1}),1.0]])]});}
            var Q47;
            {var subQ0=sQuery(id+"F0.wireOp",EDGE,"E4.16.0");var subQ1=sQuery(id+"F0.wireOp",EDGE,"E1");var subQ2=makeQuery(id+"F0.imprint","INTERSECT",VERTEX,{"disambiguationData":[OD(1.0)],"derivedFrom":[subQ1,subQ0]});Q47=makeQuery(id+"F0.imprint","IMPRINT",FACE,{"disambiguationData":[TD([[makeQuery(id+"F0.imprint","IMPRINT",EDGE,{"disambiguationData":[TD([[subQ2,-1.0]])],"derivedFrom":subQ1}),-1.0]])]});}
            var Q48;
            {var subQ0=sQuery(id+"F0.wireOp",EDGE,"E4.18.0");var subQ1=sQuery(id+"F0.wireOp",EDGE,"E1");var subQ2=makeQuery(id+"F0.imprint","INTERSECT",VERTEX,{"disambiguationData":[OD(1.0)],"derivedFrom":[subQ1,subQ0]});Q48=makeQuery(id+"F0.imprint","IMPRINT",FACE,{"disambiguationData":[TD([[makeQuery(id+"F0.imprint","IMPRINT",EDGE,{"disambiguationData":[TD([[subQ2,-1.0]])],"derivedFrom":subQ1}),1.0]])]});}
            var Q49;
            {var subQ0=sQuery(id+"F0.wireOp",EDGE,"E4.25.0");var subQ1=sQuery(id+"F0.wireOp",EDGE,"E1");var subQ2=makeQuery(id+"F0.imprint","INTERSECT",VERTEX,{"disambiguationData":[OD(0.0)],"derivedFrom":[subQ1,subQ0]});Q49=makeQuery(id+"F0.imprint","IMPRINT",FACE,{"disambiguationData":[TD([[makeQuery(id+"F0.imprint","IMPRINT",EDGE,{"disambiguationData":[TD([[subQ2,-1.0]])],"derivedFrom":subQ1}),-1.0]])]});}
            var Q50;
            {var subQ0=sQuery(id+"F0.wireOp",EDGE,"E4.19.0");var subQ1=sQuery(id+"F0.wireOp",EDGE,"E1");var subQ2=makeQuery(id+"F0.imprint","INTERSECT",VERTEX,{"disambiguationData":[OD(1.0)],"derivedFrom":[subQ1,subQ0]});Q50=makeQuery(id+"F0.imprint","IMPRINT",FACE,{"disambiguationData":[TD([[makeQuery(id+"F0.imprint","IMPRINT",EDGE,{"disambiguationData":[TD([[subQ2,-1.0]])],"derivedFrom":subQ1}),1.0]])]});}
            var Q51;
            {var subQ0=sQuery(id+"F0.wireOp",EDGE,"E4.19.0");var subQ1=sQuery(id+"F0.wireOp",EDGE,"E1");var subQ2=makeQuery(id+"F0.imprint","INTERSECT",VERTEX,{"disambiguationData":[OD(0.0)],"derivedFrom":[subQ1,subQ0]});Q51=makeQuery(id+"F0.imprint","IMPRINT",FACE,{"disambiguationData":[TD([[makeQuery(id+"F0.imprint","IMPRINT",EDGE,{"disambiguationData":[TD([[subQ2,-1.0]])],"derivedFrom":subQ1}),1.0]])]});}
            var Q52;
            {var subQ0=sQuery(id+"F0.wireOp",EDGE,"E4.20.0");var subQ1=sQuery(id+"F0.wireOp",EDGE,"E1");var subQ2=makeQuery(id+"F0.imprint","INTERSECT",VERTEX,{"disambiguationData":[OD(0.0)],"derivedFrom":[subQ1,subQ0]});Q52=makeQuery(id+"F0.imprint","IMPRINT",FACE,{"disambiguationData":[TD([[makeQuery(id+"F0.imprint","IMPRINT",EDGE,{"disambiguationData":[TD([[subQ2,-1.0]])],"derivedFrom":subQ1}),1.0]])]});}
            var Q53;
            {var subQ0=sQuery(id+"F0.wireOp",EDGE,"E4.22.0");var subQ1=sQuery(id+"F0.wireOp",EDGE,"E1");var subQ2=makeQuery(id+"F0.imprint","INTERSECT",VERTEX,{"disambiguationData":[OD(0.0)],"derivedFrom":[subQ1,subQ0]});Q53=makeQuery(id+"F0.imprint","IMPRINT",FACE,{"disambiguationData":[TD([[makeQuery(id+"F0.imprint","IMPRINT",EDGE,{"disambiguationData":[TD([[subQ2,-1.0]])],"derivedFrom":subQ1}),-1.0]])]});}
            var Q54;
            {var subQ0=sQuery(id+"F0.wireOp",EDGE,"E4.24.0");var subQ1=sQuery(id+"F0.wireOp",EDGE,"E1");var subQ2=makeQuery(id+"F0.imprint","INTERSECT",VERTEX,{"disambiguationData":[OD(1.0)],"derivedFrom":[subQ1,subQ0]});Q54=makeQuery(id+"F0.imprint","IMPRINT",FACE,{"disambiguationData":[TD([[makeQuery(id+"F0.imprint","IMPRINT",EDGE,{"disambiguationData":[TD([[subQ2,-1.0]])],"derivedFrom":subQ1}),1.0]])]});}
            var Q55;
            {var subQ0=sQuery(id+"F0.wireOp",EDGE,"E4.20.0");var subQ1=sQuery(id+"F0.wireOp",EDGE,"E1");var subQ2=makeQuery(id+"F0.imprint","INTERSECT",VERTEX,{"disambiguationData":[OD(1.0)],"derivedFrom":[subQ1,subQ0]});Q55=makeQuery(id+"F0.imprint","IMPRINT",FACE,{"disambiguationData":[TD([[makeQuery(id+"F0.imprint","IMPRINT",EDGE,{"disambiguationData":[TD([[subQ2,-1.0]])],"derivedFrom":subQ1}),1.0]])]});}
            var Q56;
            {var subQ0=sQuery(id+"F0.wireOp",EDGE,"E4.30.0");var subQ1=sQuery(id+"F0.wireOp",EDGE,"E1");var subQ2=makeQuery(id+"F0.imprint","INTERSECT",VERTEX,{"disambiguationData":[OD(0.0)],"derivedFrom":[subQ1,subQ0]});Q56=makeQuery(id+"F0.imprint","IMPRINT",FACE,{"disambiguationData":[TD([[makeQuery(id+"F0.imprint","IMPRINT",EDGE,{"disambiguationData":[TD([[subQ2,-1.0]])],"derivedFrom":subQ1}),1.0]])]});}
            var Q57;
            {var subQ0=sQuery(id+"F0.wireOp",EDGE,"E4.24.0");var subQ1=sQuery(id+"F0.wireOp",EDGE,"E1");var subQ2=makeQuery(id+"F0.imprint","INTERSECT",VERTEX,{"disambiguationData":[OD(0.0)],"derivedFrom":[subQ1,subQ0]});Q57=makeQuery(id+"F0.imprint","IMPRINT",FACE,{"disambiguationData":[TD([[makeQuery(id+"F0.imprint","IMPRINT",EDGE,{"disambiguationData":[TD([[subQ2,-1.0]])],"derivedFrom":subQ1}),-1.0]])]});}
            var Q58;
            {var subQ0=sQuery(id+"F0.wireOp",EDGE,"E4.29.0");var subQ1=sQuery(id+"F0.wireOp",EDGE,"E1");var subQ2=makeQuery(id+"F0.imprint","INTERSECT",VERTEX,{"disambiguationData":[OD(1.0)],"derivedFrom":[subQ1,subQ0]});Q58=makeQuery(id+"F0.imprint","IMPRINT",FACE,{"disambiguationData":[TD([[makeQuery(id+"F0.imprint","IMPRINT",EDGE,{"disambiguationData":[TD([[subQ2,-1.0]])],"derivedFrom":subQ1}),-1.0]])]});}
            var Q59;
            {var subQ0=sQuery(id+"F0.wireOp",EDGE,"E4.26.0");var subQ1=sQuery(id+"F0.wireOp",EDGE,"E1");var subQ2=makeQuery(id+"F0.imprint","INTERSECT",VERTEX,{"disambiguationData":[OD(1.0)],"derivedFrom":[subQ1,subQ0]});Q59=makeQuery(id+"F0.imprint","IMPRINT",FACE,{"disambiguationData":[TD([[makeQuery(id+"F0.imprint","IMPRINT",EDGE,{"disambiguationData":[TD([[subQ2,-1.0]])],"derivedFrom":subQ1}),1.0]])]});}
            var Q60;
            {var subQ0=sQuery(id+"F0.wireOp",EDGE,"E4.21.0");var subQ1=sQuery(id+"F0.wireOp",EDGE,"E1");var subQ2=makeQuery(id+"F0.imprint","INTERSECT",VERTEX,{"disambiguationData":[OD(0.0)],"derivedFrom":[subQ1,subQ0]});Q60=makeQuery(id+"F0.imprint","IMPRINT",FACE,{"disambiguationData":[TD([[makeQuery(id+"F0.imprint","IMPRINT",EDGE,{"disambiguationData":[TD([[subQ2,-1.0]])],"derivedFrom":subQ1}),-1.0]])]});}
            var Q61;
            {var subQ0=sQuery(id+"F0.wireOp",EDGE,"E4.23.0");var subQ1=sQuery(id+"F0.wireOp",EDGE,"E1");var subQ2=makeQuery(id+"F0.imprint","INTERSECT",VERTEX,{"disambiguationData":[OD(0.0)],"derivedFrom":[subQ1,subQ0]});Q61=makeQuery(id+"F0.imprint","IMPRINT",FACE,{"disambiguationData":[TD([[makeQuery(id+"F0.imprint","IMPRINT",EDGE,{"disambiguationData":[TD([[subQ2,-1.0]])],"derivedFrom":subQ1}),1.0]])]});}
            var Q62;
            {var subQ0=sQuery(id+"F0.wireOp",EDGE,"E4.30.0");var subQ1=sQuery(id+"F0.wireOp",EDGE,"E1");var subQ2=makeQuery(id+"F0.imprint","INTERSECT",VERTEX,{"disambiguationData":[OD(0.0)],"derivedFrom":[subQ1,subQ0]});Q62=makeQuery(id+"F0.imprint","IMPRINT",FACE,{"disambiguationData":[TD([[makeQuery(id+"F0.imprint","IMPRINT",EDGE,{"disambiguationData":[TD([[subQ2,-1.0]])],"derivedFrom":subQ1}),-1.0]])]});}
            var Q63;
            {var subQ0=sQuery(id+"F0.wireOp",EDGE,"E4.30.0");var subQ1=sQuery(id+"F0.wireOp",EDGE,"E1");var subQ2=makeQuery(id+"F0.imprint","INTERSECT",VERTEX,{"disambiguationData":[OD(1.0)],"derivedFrom":[subQ1,subQ0]});Q63=makeQuery(id+"F0.imprint","IMPRINT",FACE,{"disambiguationData":[TD([[makeQuery(id+"F0.imprint","IMPRINT",EDGE,{"disambiguationData":[TD([[subQ2,-1.0]])],"derivedFrom":subQ1}),-1.0]])]});}
            var Q64;
            {var subQ0=sQuery(id+"F0.wireOp",EDGE,"E4.23.0");var subQ1=sQuery(id+"F0.wireOp",EDGE,"E1");var subQ2=makeQuery(id+"F0.imprint","INTERSECT",VERTEX,{"disambiguationData":[OD(0.0)],"derivedFrom":[subQ1,subQ0]});Q64=makeQuery(id+"F0.imprint","IMPRINT",FACE,{"disambiguationData":[TD([[makeQuery(id+"F0.imprint","IMPRINT",EDGE,{"disambiguationData":[TD([[subQ2,-1.0]])],"derivedFrom":subQ1}),-1.0]])]});}
            var Q65;
            {var subQ0=sQuery(id+"F0.wireOp",EDGE,"E5.bottom");var subQ1=sQuery(id+"F0.wireOp",EDGE,"E0");var subQ2=makeQuery(id+"F0.imprint","INTERSECT",VERTEX,{"derivedFrom":[subQ1,subQ0]});Q65=makeQuery(id+"F0.imprint","IMPRINT",FACE,{"disambiguationData":[TD([[makeQuery(id+"F0.imprint","IMPRINT",EDGE,{"disambiguationData":[TD([[subQ2,-1.0]])],"derivedFrom":subQ1}),-1.0]])]});}
            var Q66;
            {var subQ0=sQuery(id+"F0.wireOp",EDGE,"E5.top");var subQ1=sQuery(id+"F0.wireOp",EDGE,"E0");var subQ2=makeQuery(id+"F0.imprint","INTERSECT",VERTEX,{"derivedFrom":[subQ1,subQ0]});Q66=makeQuery(id+"F0.imprint","IMPRINT",FACE,{"disambiguationData":[TD([[makeQuery(id+"F0.imprint","IMPRINT",EDGE,{"disambiguationData":[TD([[subQ2,1.0]])],"derivedFrom":subQ1}),-1.0]])]});}
            extrude(context, id + "F2", {"entities" : qUnion([Q0, Q1, Q2, Q3, Q4, Q5, Q6, Q7, Q8, Q9, Q10, Q11, Q12, Q13, Q14, Q15, Q16, Q17, Q18, Q19, Q20, Q21, Q22, Q23, Q24, Q25, Q26, Q27, Q28, Q29, Q30, Q31, Q32, Q33, Q34, Q35, Q36, Q37, Q38, Q39, Q40, Q41, Q42, Q43, Q44, Q45, Q46, Q47, Q48, Q49, Q50, Q51, Q52, Q53, Q54, Q55, Q56, Q57, Q58, Q59, Q60, Q61, Q62, Q63, Q64, Q65, Q66]), "operationType" : NewBodyOperationType.REMOVE, "endBound" : BoundingType.SYMMETRIC, "depth" : 50 * mm, "offsetDistance" : 25 * mm});
        }
        {
            var Q0;
            Q0=makeQuery(id+"F1.opExtrude","SWEPT_FACE",FACE,{"disambiguationData":[OSD([sQuery(id+"F0.wireOp",EDGE,"E5.right")])]});
            var sketch = newSketch(context, id + "F3", { "sketchPlane" : qUnion([Q0])});
            skLineSegment(sketch, "E9.bottom", {"start": v(37.5, 37.5) * mm, "end": v(-37.5, 37.5) * mm, "construction": true});
            skLineSegment(sketch, "E9.top", {"start": v(37.5, -37.5) * mm, "end": v(-37.5, -37.5) * mm, "construction": true});
            skLineSegment(sketch, "E9.left", {"start": v(37.5, 37.5) * mm, "end": v(37.5, -37.5) * mm, "construction": true});
            skLineSegment(sketch, "E9.right", {"start": v(-37.5, 37.5) * mm, "end": v(-37.5, -37.5) * mm, "construction": true});
            skPoint(sketch, "E9.middle", {"position": v(0, 0) * mm});
            skCircle(sketch, "E10", {"center": v(-37.5, 37.5) * mm, "radius": 2.5 * mm});
            skCircle(sketch, "E11", {"center": v(-37.5, -37.5) * mm, "radius": 2.5 * mm});
            skCircle(sketch, "E12", {"center": v(37.5, -37.5) * mm, "radius": 2.5 * mm});
            skCircle(sketch, "E13", {"center": v(37.5, 37.5) * mm, "radius": 2.5 * mm});
            skLineSegment(sketch, "E14.bottom", {"start": v(-25, 25) * mm, "end": v(25, 25) * mm});
            skLineSegment(sketch, "E14.top", {"start": v(-25, -25) * mm, "end": v(25, -25) * mm});
            skLineSegment(sketch, "E14.left", {"start": v(-25, 25) * mm, "end": v(-25, -25) * mm});
            skLineSegment(sketch, "E14.right", {"start": v(25, 25) * mm, "end": v(25, -25) * mm});
            skSolve(sketch);
        }
        {
            var Q0;
            Q0=makeQuery(id+"F3.imprint","IMPRINT",FACE,{"disambiguationData":[TD([[makeQuery(id+"F3.imprint","IMPRINT",EDGE,{"derivedFrom":sQuery(id+"F3.wireOp",EDGE,"E10")}),1.0]])]});
            var Q1;
            Q1=makeQuery(id+"F3.imprint","IMPRINT",FACE,{"disambiguationData":[TD([[makeQuery(id+"F3.imprint","IMPRINT",EDGE,{"derivedFrom":sQuery(id+"F3.wireOp",EDGE,"E13")}),1.0]])]});
            var Q2;
            Q2=makeQuery(id+"F3.imprint","IMPRINT",FACE,{"disambiguationData":[TD([[makeQuery(id+"F3.imprint","IMPRINT",EDGE,{"derivedFrom":sQuery(id+"F3.wireOp",EDGE,"E12")}),1.0]])]});
            var Q3;
            Q3=makeQuery(id+"F3.imprint","IMPRINT",FACE,{"disambiguationData":[TD([[makeQuery(id+"F3.imprint","IMPRINT",EDGE,{"derivedFrom":sQuery(id+"F3.wireOp",EDGE,"E11")}),1.0]])]});
            extrude(context, id + "F4", {"entities" : qUnion([Q0, Q1, Q2, Q3]), "operationType" : NewBodyOperationType.REMOVE, "oppositeDirection" : true, "depth" : 20 * mm, "offsetDistance" : 25 * mm});
        }
        {
            var Q0;
            Q0=makeQuery(id+"F3.imprint","IMPRINT",FACE,{"disambiguationData":[TD([[makeQuery(id+"F3.imprint","IMPRINT",EDGE,{"derivedFrom":sQuery(id+"F3.wireOp",EDGE,"E14.bottom")}),-1.0]])]});
            extrude(context, id + "F5", {"entities" : qUnion([Q0]), "operationType" : NewBodyOperationType.REMOVE, "endBound" : BoundingType.THROUGH_ALL, "oppositeDirection" : true, "depth" : 25 * mm, "offsetDistance" : 25 * mm});
        }
        {
            var Q0;
            Q0=makeQuery(id+"F1.opExtrude","CAP_FACE",FACE,{"disambiguationData":[OSD([sQuery(id+"F0.wireOp",EDGE,"E0"),sQuery(id+"F0.wireOp",EDGE,"E1"),sQuery(id+"F0.wireOp",EDGE,"E2"),sQuery(id+"F0.wireOp",EDGE,"E4.17.0"),sQuery(id+"F0.wireOp",EDGE,"E4.19.0"),sQuery(id+"F0.wireOp",EDGE,"E4.21.0"),sQuery(id+"F0.wireOp",EDGE,"E4.23.0"),sQuery(id+"F0.wireOp",EDGE,"E4.25.0"),sQuery(id+"F0.wireOp",EDGE,"E4.27.0"),sQuery(id+"F0.wireOp",EDGE,"E4.29.0"),sQuery(id+"F0.wireOp",EDGE,"E4.31.0"),sQuery(id+"F0.wireOp",EDGE,"E5.bottom"),sQuery(id+"F0.wireOp",EDGE,"E5.top"),sQuery(id+"F0.wireOp",EDGE,"E5.right")])],"isStart":false});
            var sketch = newSketch(context, id + "F6", { "sketchPlane" : qUnion([Q0])});
            skLineSegment(sketch, "E15.bottom", {"start": v(-55, 30) * mm, "end": v(-47, 30) * mm});
            skLineSegment(sketch, "E15.top", {"start": v(-55, 45) * mm, "end": v(-47, 45) * mm});
            skLineSegment(sketch, "E15.left", {"start": v(-55, 30) * mm, "end": v(-55, 45) * mm});
            skLineSegment(sketch, "E15.right", {"start": v(-47, 30) * mm, "end": v(-47, 45) * mm});
            skPoint(sketch, "E15.middle", {"position": v(-51, 37.5) * mm});
            skLineSegment(sketch, "E16.0.1.0", {"start": v(-55, -45) * mm, "end": v(-47, -45) * mm});
            skLineSegment(sketch, "E16.0.1.1", {"start": v(-47, -45) * mm, "end": v(-47, -30) * mm});
            skLineSegment(sketch, "E16.0.1.2", {"start": v(-55, -30) * mm, "end": v(-47, -30) * mm});
            skLineSegment(sketch, "E16.0.1.3", {"start": v(-55, -45) * mm, "end": v(-55, -30) * mm});
            skLineSegment(sketch, "E16.direction1", {"start": v(-55, 30) * mm, "end": v(-33.5, 30) * mm, "construction": true});
            skLineSegment(sketch, "E16.direction2", {"start": v(-55, 30) * mm, "end": v(-55, -45) * mm, "construction": true});
            skSolve(sketch);
        }
        {
            var Q0;
            Q0=makeQuery(id+"F6.imprint","IMPRINT",FACE,{"disambiguationData":[TD([[makeQuery(id+"F6.imprint","IMPRINT",EDGE,{"derivedFrom":sQuery(id+"F6.wireOp",EDGE,"E15.bottom")}),1.0]])]});
            var Q1;
            Q1=makeQuery(id+"F6.imprint","IMPRINT",FACE,{"disambiguationData":[TD([[makeQuery(id+"F6.imprint","IMPRINT",EDGE,{"derivedFrom":sQuery(id+"F6.wireOp",EDGE,"E16.0.1.0")}),1.0]])]});
            extrude(context, id + "F7", {"entities" : qUnion([Q0, Q1]), "operationType" : NewBodyOperationType.REMOVE, "endBound" : BoundingType.THROUGH_ALL, "oppositeDirection" : true, "depth" : 25 * mm, "offsetDistance" : 25 * mm});
        }
    });
